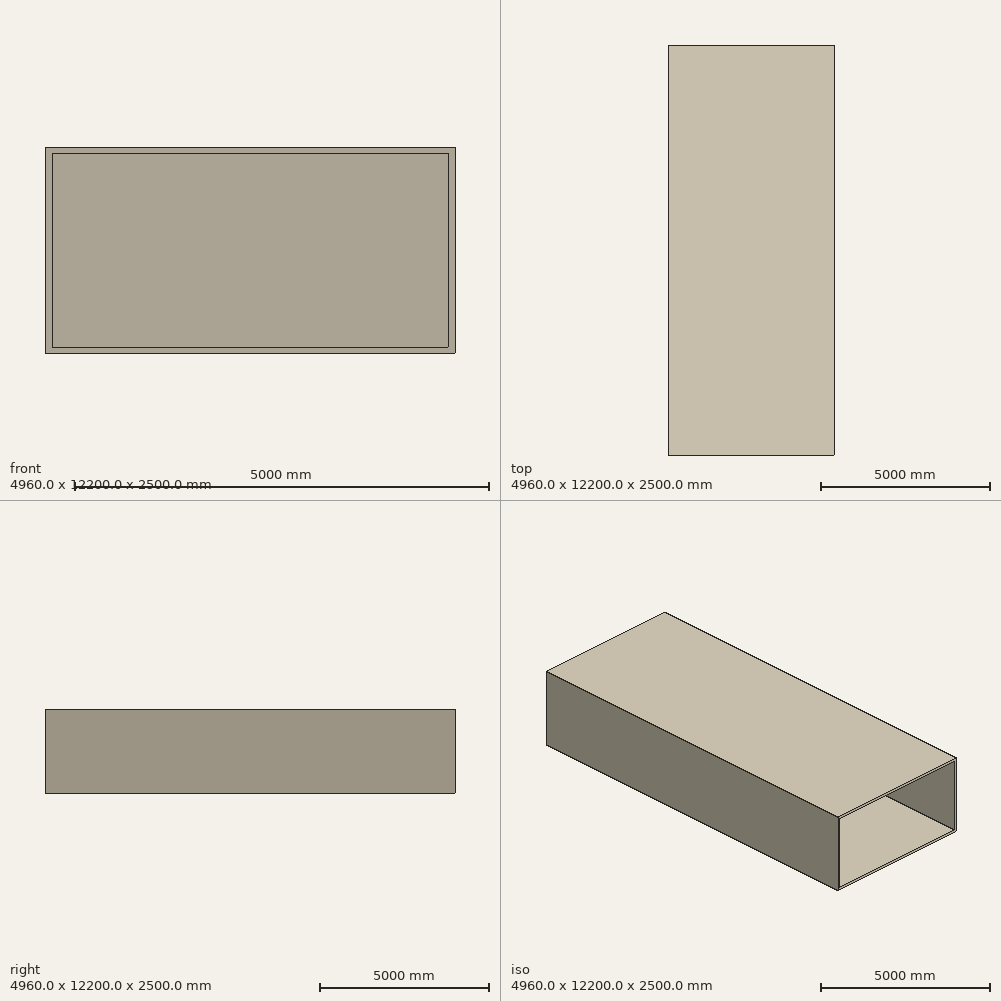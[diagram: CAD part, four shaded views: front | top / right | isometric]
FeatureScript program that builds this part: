
annotation { "Feature Type Name" : "Feature", "Feature Type Description" : "" }
export const myFeature = defineFeature(function(context is Context, id is Id, definition is map)
    precondition{}
    {
        {
            var Q0;
            Q0=qCreatedBy(makeId("Top.planeOp"),FACE);
            var sketch = newSketch(context, id + "F0", { "sketchPlane" : qUnion([Q0])});
            skLineSegment(sketch, "E0.bottom", {"start": v(-2328.18, 6105.24) * mm, "end": v(151.82, 6105.24) * mm});
            skLineSegment(sketch, "E0.top", {"start": v(-2328.18, -6094.76) * mm, "end": v(151.82, -6094.76) * mm});
            skLineSegment(sketch, "E0.left", {"start": v(-2328.18, 6105.24) * mm, "end": v(-2328.18, -6094.76) * mm});
            skLineSegment(sketch, "E0.right", {"start": v(151.82, 6105.24) * mm, "end": v(151.82, -6094.76) * mm});
            skLineSegment(sketch, "E1.0", {"start": v(71.82, 6025.24) * mm, "end": v(71.82, -6014.76) * mm});
            skLineSegment(sketch, "E1.1", {"start": v(-2248.18, 6025.24) * mm, "end": v(71.82, 6025.24) * mm});
            skLineSegment(sketch, "E1.2", {"start": v(-2248.18, 6025.24) * mm, "end": v(-2248.18, -6014.76) * mm});
            skLineSegment(sketch, "E1.3", {"start": v(-2248.18, -6014.76) * mm, "end": v(71.82, -6014.76) * mm});
            skSolve(sketch);
        }
        {
            var Q0;
            Q0 = qSketchRegion(id + "F0", true);
            var Q1;
            Q1=makeQuery(id+"F0.imprint","IMPRINT",FACE,{"disambiguationData":[TD([[makeQuery(id+"F0.imprint","IMPRINT",EDGE,{"derivedFrom":sQuery(id+"F0.wireOp",EDGE,"E1.0")}),-1.0]])]});
            extrude(context, id + "F1", {"entities" : qUnion([Q0, Q1]), "depth" : 2500 * mm, "offsetDistance" : 25 * mm});
        }
        {
            var Q0;
            Q0=makeQuery(id+"F1.opExtrude","SWEPT_BODY",BODY,{"disambiguationData":[OSD([sQuery(id+"F0.wireOp",EDGE,"E0.bottom"),sQuery(id+"F0.wireOp",EDGE,"E0.top"),sQuery(id+"F0.wireOp",EDGE,"E0.left"),sQuery(id+"F0.wireOp",EDGE,"E0.right")])]});
            var Q1;
            Q1=makeQuery(id+"F1.opExtrude","SWEPT_FACE",FACE,{"disambiguationData":[OSD([sQuery(id+"F0.wireOp",EDGE,"E0.right")])]});
            mirror(context, id + "F2", {"operationType" : NewBodyOperationType.ADD, "entities" : qUnion([Q0]), "mirrorPlane" : qUnion([Q1])});
        }
        {
            var Q0;
            {var subQ0=makeQuery(id+"F1.opExtrude","SWEPT_FACE",FACE,{"disambiguationData":[OSD([sQuery(id+"F0.wireOp",EDGE,"E0.top")])]});Q0=makeQuery(id+"F2.boolean.opBoolean","MERGE",FACE,{"derivedFrom":[subQ0,makeQuery(id+"F2.opPattern","COPY",FACE,{"derivedFrom":subQ0,"instanceName":"1"})]});}
            shell(context, id + "F3", {"entities" : qUnion([Q0]), "thickness" : 80 * mm});
        }
        {
            var Q0;
            Q0=makeQuery(id+"F2.opPattern","COPY",FACE,{"derivedFrom":makeQuery(id+"F1.opExtrude","SWEPT_FACE",FACE,{"disambiguationData":[OSD([sQuery(id+"F0.wireOp",EDGE,"E0.left")])]}),"instanceName":"1"});
            var sketch = newSketch(context, id + "F4", { "sketchPlane" : qUnion([Q0])});
            skLineSegment(sketch, "E2", {"start": v(-3559.04, 0) * mm, "end": v(-3559.04, 1714.66) * mm});
            skLineSegment(sketch, "E3", {"start": v(-3559.04, 1714.66) * mm, "end": v(-1616.28, 1714.66) * mm});
            skLineSegment(sketch, "E4", {"start": v(-1616.28, 1714.66) * mm, "end": v(-1616.28, 0) * mm});
            skSolve(sketch);
        }
    });
